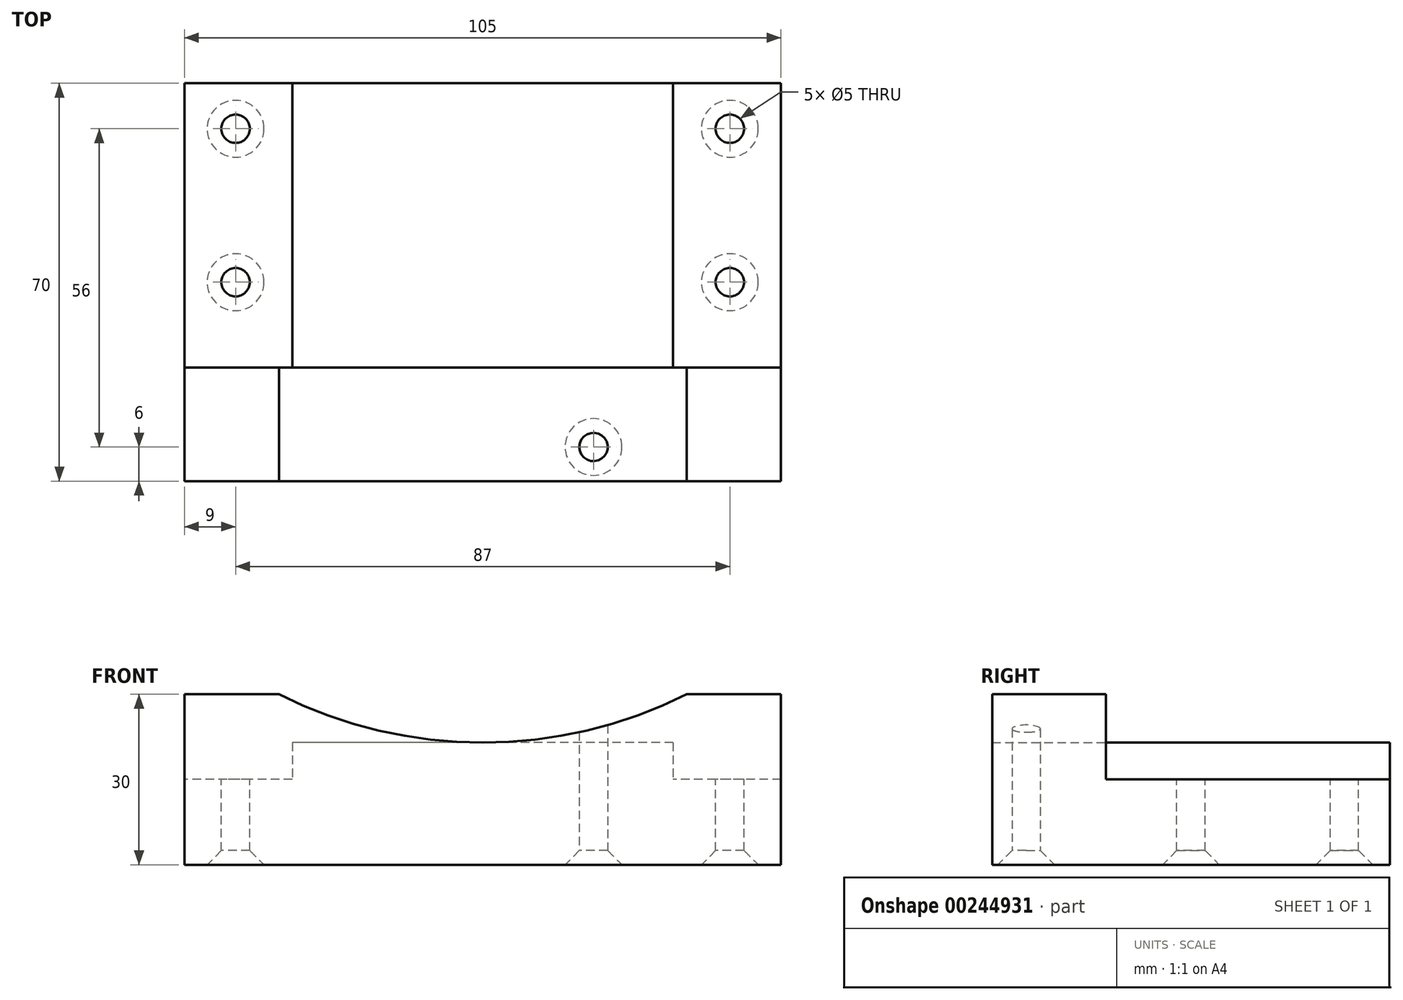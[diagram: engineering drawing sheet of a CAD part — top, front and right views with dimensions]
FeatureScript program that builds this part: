
annotation { "Feature Type Name" : "Feature", "Feature Type Description" : "" }
export const myFeature = defineFeature(function(context is Context, id is Id, definition is map)
    precondition{}
    {
        {
            var Q0;
            Q0=qCreatedBy(makeId("Top.planeOp"),FACE);
            var sketch = newSketch(context, id + "F0", { "sketchPlane" : qUnion([Q0])});
            skLineSegment(sketch, "E0.bottom", {"start": v(52.5, -35) * mm, "end": v(-52.5, -35) * mm});
            skLineSegment(sketch, "E0.top", {"start": v(52.5, 35) * mm, "end": v(-52.5, 35) * mm});
            skLineSegment(sketch, "E0.left", {"start": v(52.5, -35) * mm, "end": v(52.5, 35) * mm});
            skLineSegment(sketch, "E0.right", {"start": v(-52.5, -35) * mm, "end": v(-52.5, 35) * mm});
            skPoint(sketch, "E0.middle", {"position": v(0, 0) * mm});
            skLineSegment(sketch, "E1", {"start": v(0, 0) * mm, "end": v(43.5, 0) * mm});
            skLineSegment(sketch, "E2", {"start": v(43.5, 0) * mm, "end": v(43.5, 27) * mm});
            skCircle(sketch, "E3", {"center": v(43.5, 27) * mm, "radius": 2.5 * mm});
            skCircle(sketch, "E4", {"center": v(43.5, 0) * mm, "radius": 2.5 * mm});
            skCircle(sketch, "E5.MirrorC", {"center": v(-43.5, 27) * mm, "radius": 2.5 * mm});
            skCircle(sketch, "E6.MirrorC", {"center": v(-43.5, 0) * mm, "radius": 2.5 * mm});
            skSolve(sketch);
        }
        {
            var Q0;
            Q0 = qSketchRegion(id + "F0", true);
            extrude(context, id + "F1", {"entities" : qUnion([Q0]), "oppositeDirection" : true, "depth" : 15 * mm});
        }
        {
            var Q0;
            Q0=qCreatedBy(makeId("Top.planeOp"),FACE);
            var sketch = newSketch(context, id + "F2", { "sketchPlane" : qUnion([Q0])});
            skLineSegment(sketch, "E7", {"start": v(0, 0) * mm, "end": v(0, 10) * mm});
            skLineSegment(sketch, "E8.bottom", {"start": v(33.5, -15) * mm, "end": v(-33.5, -15) * mm});
            skLineSegment(sketch, "E8.top", {"start": v(33.5, 35) * mm, "end": v(-33.5, 35) * mm});
            skLineSegment(sketch, "E8.left", {"start": v(33.5, -15) * mm, "end": v(33.5, 35) * mm});
            skLineSegment(sketch, "E8.right", {"start": v(-33.5, -15) * mm, "end": v(-33.5, 35) * mm});
            skPoint(sketch, "E8.middle", {"position": v(0, 10) * mm});
            skSolve(sketch);
        }
        {
            var Q0;
            Q0 = qSketchRegion(id + "F2", true);
            extrude(context, id + "F3", {"entities" : qUnion([Q0]), "operationType" : NewBodyOperationType.ADD, "depth" : 6.5 * mm});
        }
        {
            var Q0;
            Q0=qCreatedBy(makeId("Top.planeOp"),FACE);
            var sketch = newSketch(context, id + "F4", { "sketchPlane" : qUnion([Q0])});
            skLineSegment(sketch, "E9", {"start": v(0, 0) * mm, "end": v(0, -25) * mm});
            skLineSegment(sketch, "E10.bottom", {"start": v(52.5, -35) * mm, "end": v(-52.5, -35) * mm});
            skLineSegment(sketch, "E10.top", {"start": v(52.5, -15) * mm, "end": v(-52.5, -15) * mm});
            skLineSegment(sketch, "E10.left", {"start": v(52.5, -35) * mm, "end": v(52.5, -15) * mm});
            skLineSegment(sketch, "E10.right", {"start": v(-52.5, -35) * mm, "end": v(-52.5, -15) * mm});
            skPoint(sketch, "E10.middle", {"position": v(0, -25) * mm});
            skSolve(sketch);
        }
        {
            var Q0;
            Q0 = qSketchRegion(id + "F4", true);
            extrude(context, id + "F5", {"entities" : qUnion([Q0]), "operationType" : NewBodyOperationType.ADD, "depth" : 15 * mm});
        }
        {
            var Q0;
            Q0=qCreatedBy(makeId("Front.planeOp"),FACE);
            var sketch = newSketch(context, id + "F6", { "sketchPlane" : qUnion([Q0])});
            skLineSegment(sketch, "E11", {"start": v(0, 0) * mm, "end": v(0, 86.5) * mm});
            skCircle(sketch, "E12", {"center": v(0, 86.5) * mm, "radius": 80 * mm});
            skSolve(sketch);
        }
        {
            var Q0;
            Q0 = qSketchRegion(id + "F6", true);
            extrude(context, id + "F7", {"entities" : qUnion([Q0]), "depth" : 40 * mm});
        }
        {
            var Q0;
            Q0=qCreatedBy(makeId("Top.planeOp"),FACE);
            var sketch = newSketch(context, id + "F8", { "sketchPlane" : qUnion([Q0])});
            skLineSegment(sketch, "E13", {"start": v(0, 0) * mm, "end": v(0, -29) * mm});
            skLineSegment(sketch, "E14", {"start": v(0, -29) * mm, "end": v(19.5, -29) * mm});
            skCircle(sketch, "E15", {"center": v(19.5, -29) * mm, "radius": 2.5 * mm});
            skCircle(sketch, "E16.MirrorC", {"center": v(-19.5, -29) * mm, "radius": 2.5 * mm});
            skSolve(sketch);
        }
        {
            var Q0;
            {Q0=qUnion([makeQuery(id+"F8.imprint","IMPRINT",FACE,{"disambiguationData":[TD([[makeQuery(id+"F8.imprint","IMPRINT",EDGE,{"derivedFrom":sQuery(id+"F8.wireOp",EDGE,"E15")}),1.0]])]}),makeQuery(id+"F8.imprint","IMPRINT",FACE,{"disambiguationData":[TD([[makeQuery(id+"F8.imprint","IMPRINT",EDGE,{"derivedFrom":sQuery(id+"F8.wireOp",EDGE,"E16.MirrorC")}),-1.0]])]})]);}
            extrude(context, id + "F9", {"entities" : qUnion([Q0]), "endBound" : BoundingType.SYMMETRIC, "depth" : 40 * mm});
        }
        {
            var Q0;
            Q0=makeQuery(id+"F7.opExtrude","SWEPT_BODY",BODY,{"disambiguationData":[OSD([sQuery(id+"F6.wireOp",EDGE,"E12")])]});
            var Q1;
            Q1=makeQuery(id+"F9.opExtrude","SWEPT_BODY",BODY,{"disambiguationData":[OSD([sQuery(id+"F8.wireOp",EDGE,"E15")])]});
            var Q2;
            Q2=makeQuery(id+"F9.opExtrude","SWEPT_BODY",BODY,{"disambiguationData":[OSD([sQuery(id+"F8.wireOp",EDGE,"E16.MirrorC")])]});
            var Q3;
            Q3=makeQuery(id+"F1.opExtrude","SWEPT_BODY",BODY,{"disambiguationData":[OSD([sQuery(id+"F0.wireOp",EDGE,"E0.bottom"),sQuery(id+"F0.wireOp",EDGE,"E0.top"),sQuery(id+"F0.wireOp",EDGE,"E0.left"),sQuery(id+"F0.wireOp",EDGE,"E0.right"),sQuery(id+"F0.wireOp",EDGE,"E3"),sQuery(id+"F0.wireOp",EDGE,"E4"),sQuery(id+"F0.wireOp",EDGE,"E5.MirrorC"),sQuery(id+"F0.wireOp",EDGE,"E6.MirrorC")])]});
            booleanBodies(context, id + "F10", {"operationType" : BooleanOperationType.SUBTRACTION, "tools" : qUnion([Q0, Q1, Q2]), "targets" : qUnion([Q3])});
        }
        {
            var Q0;
            Q0=makeQuery(id+"F1.opExtrude","CAP_EDGE",EDGE,{"disambiguationData":[OSD([sQuery(id+"F0.wireOp",EDGE,"E6.MirrorC")])],"isStart":false});
            var Q1;
            Q1=makeQuery(id+"F1.opExtrude","CAP_EDGE",EDGE,{"disambiguationData":[OSD([sQuery(id+"F0.wireOp",EDGE,"E5.MirrorC")])],"isStart":false});
            var Q2;
            Q2=makeQuery(id+"F10.opBoolean","INTERSECT",EDGE,{"derivedFrom":[makeQuery(id+"F1.opExtrude","CAP_FACE",FACE,{"disambiguationData":[OSD([sQuery(id+"F0.wireOp",EDGE,"E0.bottom"),sQuery(id+"F0.wireOp",EDGE,"E0.top"),sQuery(id+"F0.wireOp",EDGE,"E0.left"),sQuery(id+"F0.wireOp",EDGE,"E0.right"),sQuery(id+"F0.wireOp",EDGE,"E3"),sQuery(id+"F0.wireOp",EDGE,"E4"),sQuery(id+"F0.wireOp",EDGE,"E5.MirrorC"),sQuery(id+"F0.wireOp",EDGE,"E6.MirrorC")])],"isStart":false}),makeQuery(id+"F9.opExtrude","SWEPT_FACE",FACE,{"disambiguationData":[OSD([sQuery(id+"F8.wireOp",EDGE,"E16.MirrorC")])]})]});
            var Q3;
            Q3=makeQuery(id+"F10.opBoolean","INTERSECT",EDGE,{"derivedFrom":[makeQuery(id+"F1.opExtrude","CAP_FACE",FACE,{"disambiguationData":[OSD([sQuery(id+"F0.wireOp",EDGE,"E0.bottom"),sQuery(id+"F0.wireOp",EDGE,"E0.top"),sQuery(id+"F0.wireOp",EDGE,"E0.left"),sQuery(id+"F0.wireOp",EDGE,"E0.right"),sQuery(id+"F0.wireOp",EDGE,"E3"),sQuery(id+"F0.wireOp",EDGE,"E4"),sQuery(id+"F0.wireOp",EDGE,"E5.MirrorC"),sQuery(id+"F0.wireOp",EDGE,"E6.MirrorC")])],"isStart":false}),makeQuery(id+"F9.opExtrude","SWEPT_FACE",FACE,{"disambiguationData":[OSD([sQuery(id+"F8.wireOp",EDGE,"E15")])]})]});
            var Q4;
            Q4=makeQuery(id+"F1.opExtrude","CAP_EDGE",EDGE,{"disambiguationData":[OSD([sQuery(id+"F0.wireOp",EDGE,"E4")])],"isStart":false});
            var Q5;
            Q5=makeQuery(id+"F1.opExtrude","CAP_EDGE",EDGE,{"disambiguationData":[OSD([sQuery(id+"F0.wireOp",EDGE,"E3")])],"isStart":false});
            chamfer(context, id + "F11", {"entities" : qUnion([Q0, Q1, Q2, Q3, Q4, Q5]), "width" : 2.5 * mm, "tangentPropagation" : true});
        }
    });
